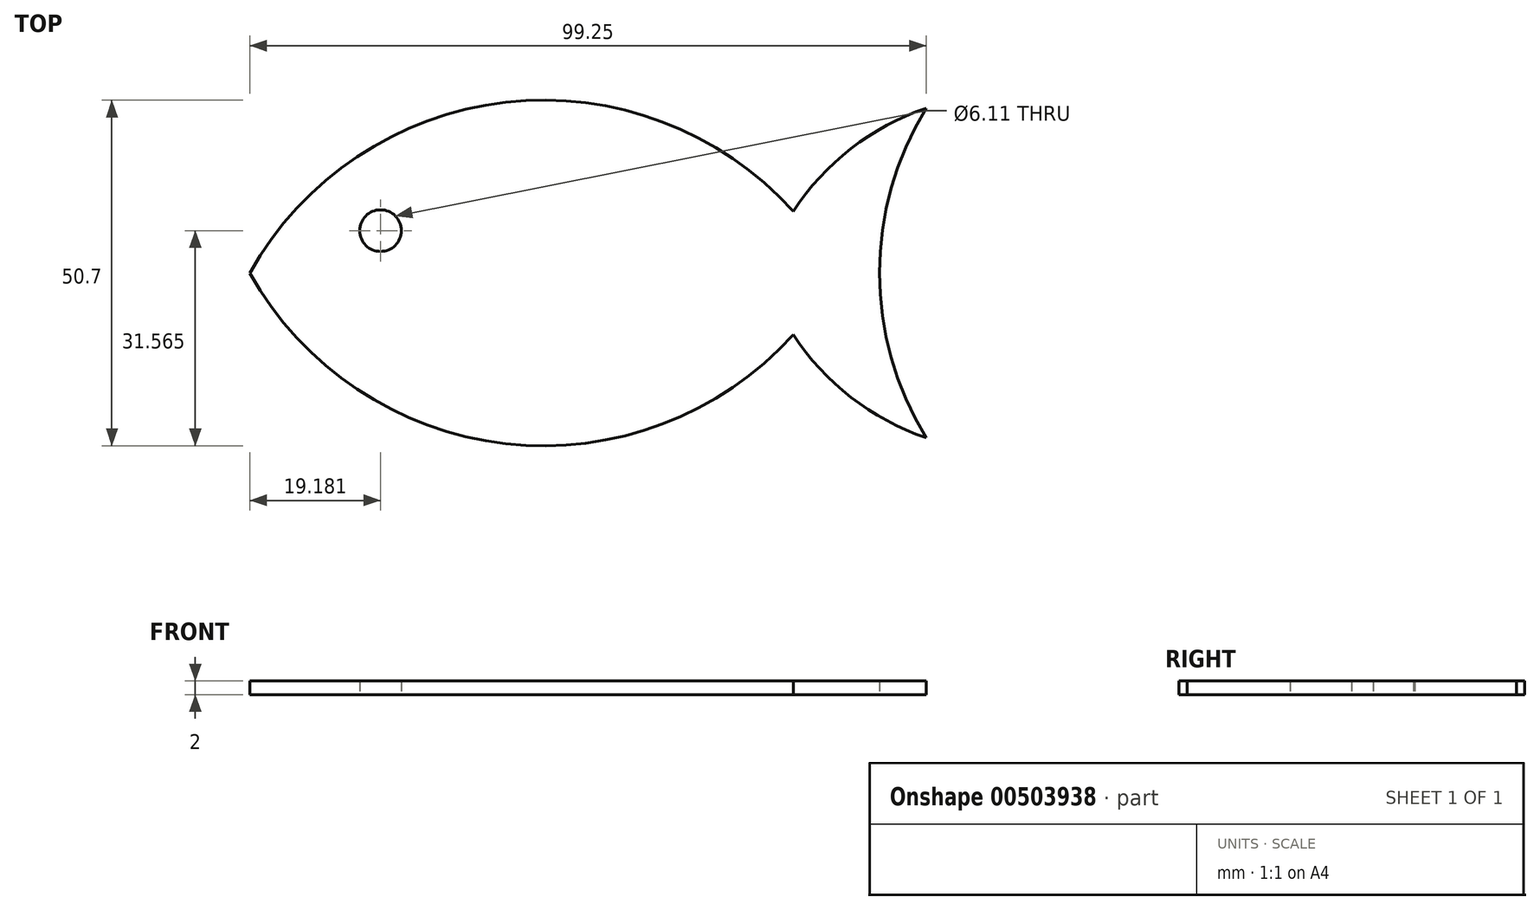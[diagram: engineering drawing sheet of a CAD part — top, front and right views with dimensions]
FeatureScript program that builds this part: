
annotation { "Feature Type Name" : "Feature", "Feature Type Description" : "" }
export const myFeature = defineFeature(function(context is Context, id is Id, definition is map)
    precondition{}
    {
        {
            var Q0;
            Q0=qCreatedBy(makeId("Top.planeOp"),FACE);
            var sketch = newSketch(context, id + "F0", { "sketchPlane" : qUnion([Q0])});
            skLineSegment(sketch, "E0", {"start": v(0, 0) * mm, "end": v(-79.73, 0) * mm, "construction": true});
            skArc(sketch, "E1", {"start": v(0, 9.06) * mm, "mid": v(-42.2, 25.04) * mm, "end": v(-79.73, 0) * mm});
            skArc(sketch, "E2", {"start": v(19.52, 24.17) * mm, "mid": v(8.5, 18.25) * mm, "end": v(0, 9.06) * mm});
            skArc(sketch, "E3.MirrorCS", {"start": v(0, -9.06) * mm, "mid": v(-42.2, -25.04) * mm, "end": v(-79.73, 0) * mm});
            skArc(sketch, "E4.MirrorCS", {"start": v(19.52, -24.17) * mm, "mid": v(8.5, -18.25) * mm, "end": v(0, -9.06) * mm});
            skArc(sketch, "E5", {"start": v(19.52, 24.17) * mm, "mid": v(12.67, 0) * mm, "end": v(19.52, -24.17) * mm});
            skCircle(sketch, "E6", {"center": v(-60.55, 6.21) * mm, "radius": 3.05 * mm});
            skSolve(sketch);
        }
        {
            var Q0;
            Q0=makeQuery(id+"F0.imprint","IMPRINT",FACE,{"disambiguationData":[TD([[makeQuery(id+"F0.imprint","IMPRINT",EDGE,{"derivedFrom":sQuery(id+"F0.wireOp",EDGE,"E1")}),1.0]])]});
            extrude(context, id + "F1", {"entities" : qUnion([Q0]), "depth" : 2 * mm});
        }
    });
